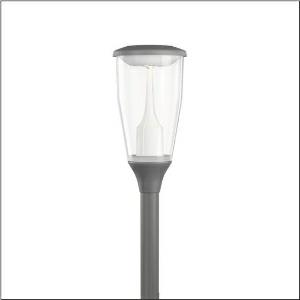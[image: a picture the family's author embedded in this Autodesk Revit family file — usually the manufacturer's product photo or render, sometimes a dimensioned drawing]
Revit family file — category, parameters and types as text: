
# Revit family: dl_11_iq___p1_0a_5xa5575bf14h000022_7e97
name_source: partatom
category: Lighting Fixtures
units: mm (PartAtom-declared; Revit-internal decimal feet)

## family parameters
Cut with Voids When Loaded = No
Host = Face
Light Source = No
Part Type = Normal
Room Calculation Point = No
Round Connector Dimension = Use Diameter
Shared = No

## types (1)
- --- (1 x LED, 1530 lm, 12.9 W, 2200K)
    Apparent Load = 13 VA
    CIE Flux Codes = 34 63 91 95 100
    Color Rendering = 70
    Color Temperature = 2200K
    Default Elevation = 1800 mm
    Description = DL 11 iQ, mast luminaire, Module 540 iQ-SR, primary light control with 3 zone facetted reflector, of plastic, silver coated, highly specular, structured, primary optical cover: cover, of PMMA, transparent, light distribution: P1.0a, light emission: direct distribution, primary light characteristic: asymmetric, installation type: post-top, LED, High Power LED, rated luminous flux: 1.560lm, luminous efficacy: 149lm/W, light colour: 722, colour temperature: 2200K, control gear: iQ Street-Remote, control: Street-Remote, Auto-Match, Temp-Guard, Lumen-Switch, Night-Set, Smart-Wire, Light-Fading, Desk-Remote (wireless, voltage-free reading and setting of iQ features in the workshop via application-optimized NFC function/RFID function), optimised constant luminous flux control (CLO 2.0), mains connection: 220..240V, AC, 50/60Hz, connection cable pre-assembled, cable length: 5,5m, wiring characteristics: H07RN-F, 5-core, 1.5mm², start of lifetime: 13W, end of service life: 13W, reduction: 5W, luminaire housing, upper part, of diecast aluminium, coated, Siteco® metallic grey (DB 702S), spigot size: 76mm (post-top), mounting height: 3..5m, post-top mast mounting element, of diecast aluminium, coated, Siteco® metallic grey (DB 702S), Module 540 iQ-SR, traffic white (RAL 9016), equipment: standard, protection rating (complete): IP66, insulation class (complete): insulation class II (safety insulation), certification: CE, ENEC, ENEC+, VDE, impact resistance: IK07, packaging unit: 1 piece

Light Distribution: P1.0a
    Height = 665 mm
    Lamp = 1 x LED
    Lamp Light Flux = 1530 lm
    Lamp Power = 12.9 W
    Lamp count = 1
    Length = 334 mm
    Luminous efficacy = 119 lm/W
    Manufacturer = Siteco
    ModVariant = No
    Model = 5XA5575BF14H000022
    Number of Poles = 1
    OnlyDefault = Yes
    Power Factor = 1
    Product Name = DL 11 iQ | P1.0a
    Product group = mast luminaire | pylon top
    ProductGroupID = 6100
    Protection Class = Protection class II
    Protection Degree = IP 66
    RLX_Detail_Level = 1
    RLX_Emergency_Light_Flux = 0 lm
    RLX_Emergency_Type = 0
    RLX_Emergency_Type_DB = No
    RlxData = <blob elided: 104925 chars, md5=491e56a8>
    Socket = socket
    Standby Power = 0 W
    System Light Flux = 1530 lm
    System Power = 13 W
    Type Comments = factory setting: luminous flux: 100 % | dim-lin: 254 | 516 mA
    Type Image = l_1258354.jpg
    URL = http://relux.com
    VarID = @adj_113313
    Voltage = 0 V
    Weight = 0.00 kg
    Width = 0 mm  [stored 0 ft]

note: [stored X ft] marks values corroborated as IEEE doubles in the binary element streams (Revit-internal decimal feet)

## geometry (parser evidence)
native form markers: Blend x4, Sweep x8
no freeform markers — native parametric forms only
